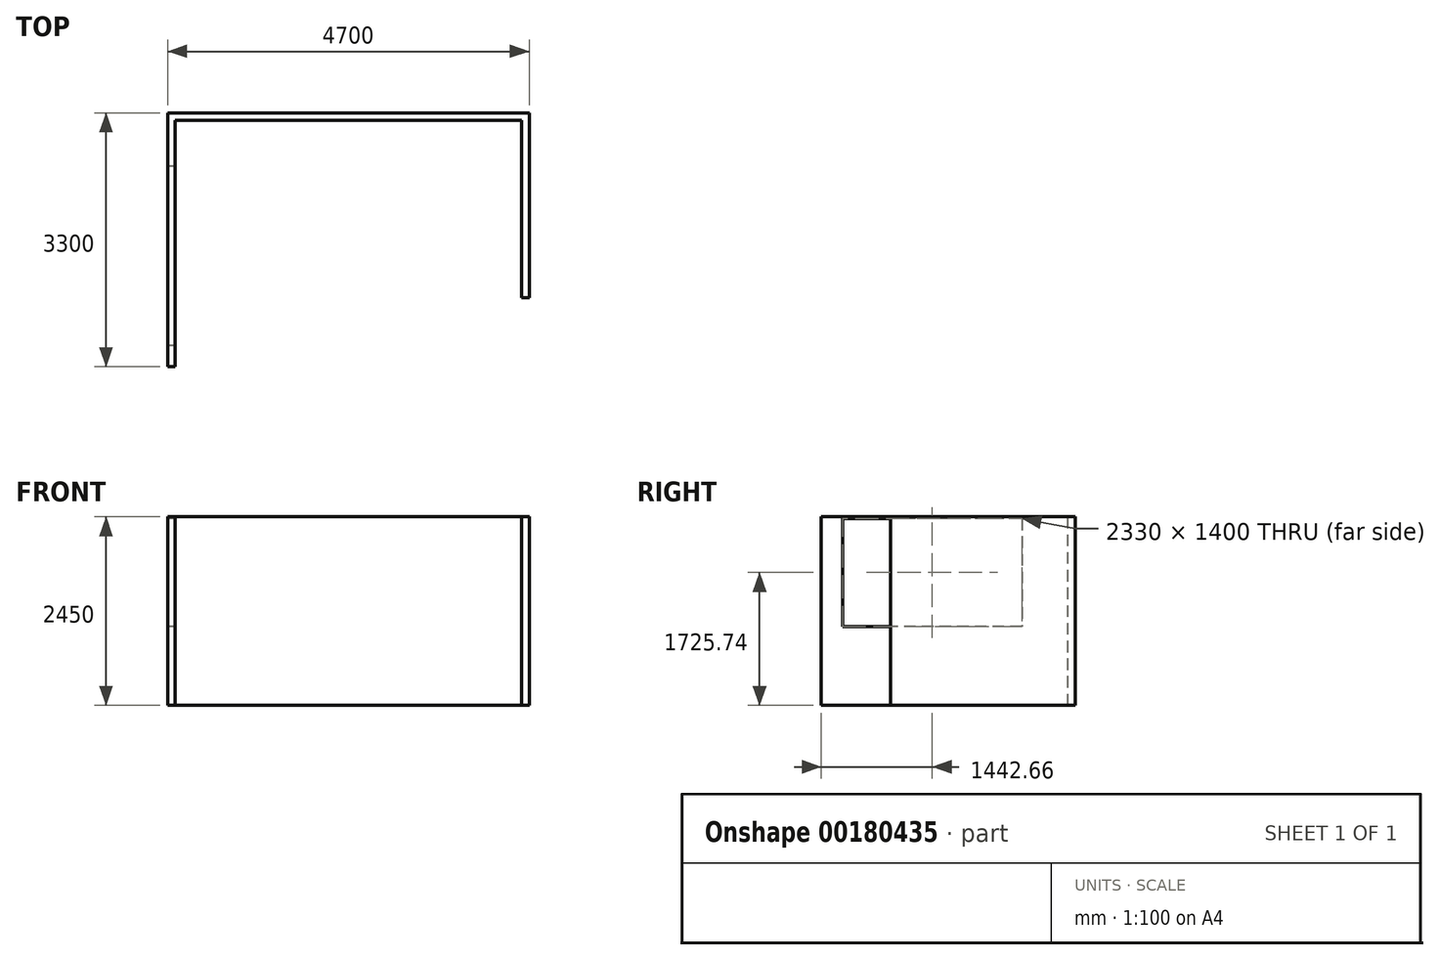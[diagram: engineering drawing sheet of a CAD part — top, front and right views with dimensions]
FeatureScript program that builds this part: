
annotation { "Feature Type Name" : "Feature", "Feature Type Description" : "" }
export const myFeature = defineFeature(function(context is Context, id is Id, definition is map)
    precondition{}
    {
        {
            var Q0;
            Q0=qCreatedBy(makeId("Top.planeOp"),FACE);
            var sketch = newSketch(context, id + "F0", { "sketchPlane" : qUnion([Q0])});
            skLineSegment(sketch, "E0", {"start": v(-148.33, -78.75) * mm, "end": v(-48.33, -78.75) * mm});
            skLineSegment(sketch, "E1", {"start": v(-48.33, -78.75) * mm, "end": v(-48.33, 3121.25) * mm});
            skLineSegment(sketch, "E2", {"start": v(-148.33, -78.75) * mm, "end": v(-148.33, 3221.25) * mm});
            skLineSegment(sketch, "E3", {"start": v(-48.33, 3121.25) * mm, "end": v(4451.67, 3121.25) * mm});
            skLineSegment(sketch, "E4", {"start": v(-148.33, 3221.25) * mm, "end": v(4551.67, 3221.25) * mm});
            skLineSegment(sketch, "E5", {"start": v(4451.67, 3121.25) * mm, "end": v(4451.67, 821.25) * mm});
            skLineSegment(sketch, "E6", {"start": v(4551.67, 3221.25) * mm, "end": v(4551.67, 821.25) * mm});
            skLineSegment(sketch, "E7", {"start": v(4451.67, 821.25) * mm, "end": v(4551.67, 821.25) * mm});
            skSolve(sketch);
        }
        {
            var Q0;
            Q0=makeQuery(id+"F0.imprint","IMPRINT",FACE,{"disambiguationData":[TD([[makeQuery(id+"F0.imprint","IMPRINT",EDGE,{"derivedFrom":sQuery(id+"F0.wireOp",EDGE,"E0")}),1.0]])]});
            extrude(context, id + "F1", {"entities" : qUnion([Q0]), "depth" : 2450 * mm});
        }
        {
            var Q0;
            Q0=makeQuery(id+"F1.opExtrude","SWEPT_FACE",FACE,{"disambiguationData":[OSD([sQuery(id+"F0.wireOp",EDGE,"E2")])]});
            var sketch = newSketch(context, id + "F2", { "sketchPlane" : qUnion([Q0])});
            skLineSegment(sketch, "E8.bottom", {"start": v(-2528.9, 2425.74) * mm, "end": v(-198.9, 2425.74) * mm});
            skLineSegment(sketch, "E8.top", {"start": v(-2528.9, 1025.74) * mm, "end": v(-198.9, 1025.74) * mm});
            skLineSegment(sketch, "E8.left", {"start": v(-2528.9, 2425.74) * mm, "end": v(-2528.9, 1025.74) * mm});
            skLineSegment(sketch, "E8.right", {"start": v(-198.9, 2425.74) * mm, "end": v(-198.9, 1025.74) * mm});
            skSolve(sketch);
        }
        {
            var Q0;
            Q0=makeQuery(id+"F2.imprint","IMPRINT",FACE,{"disambiguationData":[TD([[makeQuery(id+"F2.imprint","IMPRINT",EDGE,{"derivedFrom":sQuery(id+"F2.wireOp",EDGE,"E8.bottom")}),-1.0]])]});
            extrude(context, id + "F3", {"entities" : qUnion([Q0]), "operationType" : NewBodyOperationType.REMOVE, "oppositeDirection" : true, "depth" : 100 * mm});
        }
    });
